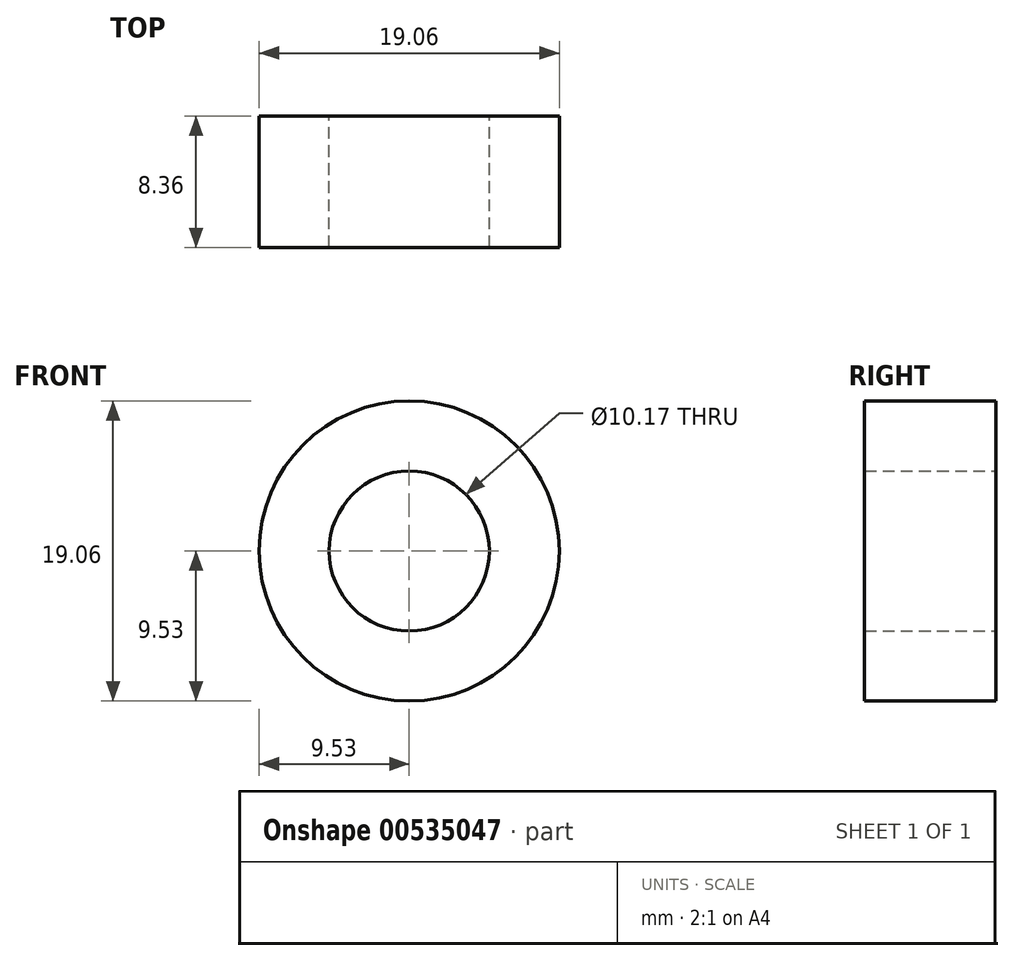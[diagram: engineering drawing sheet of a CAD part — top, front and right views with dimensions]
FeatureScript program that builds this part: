
annotation { "Feature Type Name" : "Feature", "Feature Type Description" : "" }
export const myFeature = defineFeature(function(context is Context, id is Id, definition is map)
    precondition{}
    {
        {
            var Q0;
            Q0=qCreatedBy(makeId("Front.planeOp"),FACE);
            var sketch = newSketch(context, id + "F0", { "sketchPlane" : qUnion([Q0])});
            skCircle(sketch, "E0", {"center": v(0, 0) * mm, "radius": 9.53 * mm});
            skCircle(sketch, "E1", {"center": v(0, 0) * mm, "radius": 5.08 * mm});
            skSolve(sketch);
        }
        {
            var Q0;
            Q0=makeQuery(id+"F0.imprint","IMPRINT",FACE,{"disambiguationData":[TD([[makeQuery(id+"F0.imprint","IMPRINT",EDGE,{"derivedFrom":sQuery(id+"F0.wireOp",EDGE,"E0")}),1.0]])]});
            extrude(context, id + "F1", {"entities" : qUnion([Q0]), "endBound" : BoundingType.SYMMETRIC, "depth" : 8.35 * mm, "offsetDistance" : 25 * mm});
        }
    });
